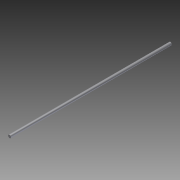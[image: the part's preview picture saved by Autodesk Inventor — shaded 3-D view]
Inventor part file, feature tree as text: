
AUTODESK INVENTOR PART (.ipt)
format: ipt  version: 2012 (Build 160160000, 160)  size: 61,952 bytes
history: native  units: in
note: dims shown in document units (in); Inventor stores cm internally (conversion verified against a paired STEP export)
features: extrude x1, sketch x1
ambient origin geometry x8: Origin, YZ Plane, XZ Plane, XY Plane, X Axis, Y Axis, Z Axis, Center Point
bodies: Solid1 (feature_tree)
feature tree (2):
  extrude  "Extrusion1"  Depth=27.5in TaperAngle=0.0deg
  sketch  "Sketch1"  dims[d0=0.5in d1=27.5in d2=0.0in]
